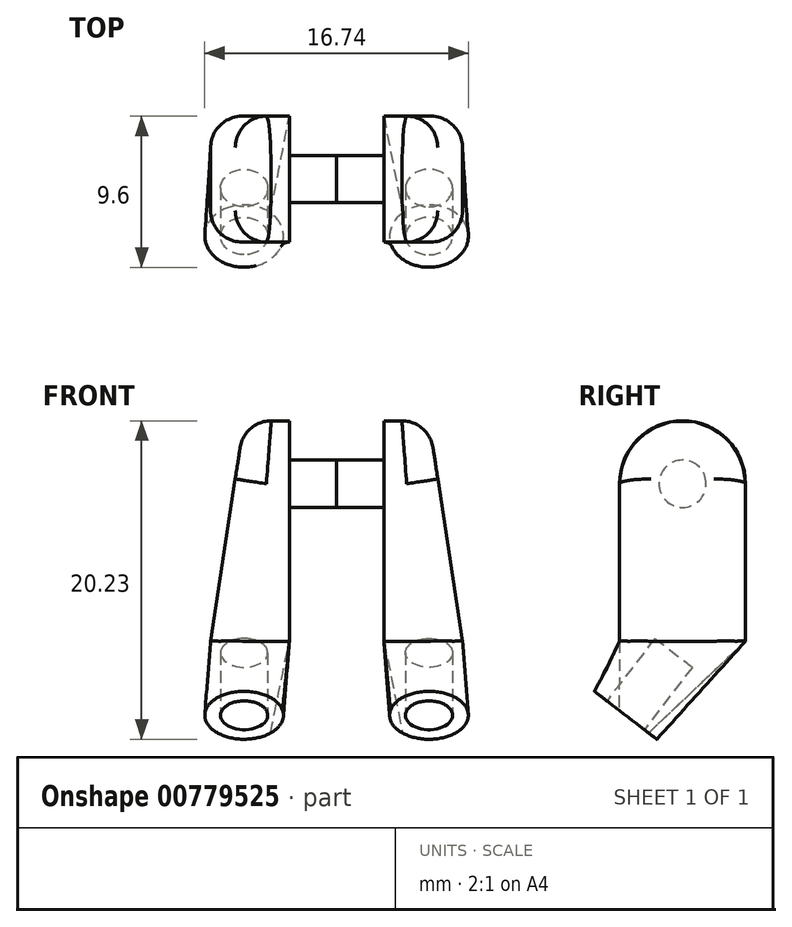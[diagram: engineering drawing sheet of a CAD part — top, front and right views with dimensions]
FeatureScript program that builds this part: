
annotation { "Feature Type Name" : "Feature", "Feature Type Description" : "" }
export const myFeature = defineFeature(function(context is Context, id is Id, definition is map)
    precondition{}
    {
        {
            var Q0;
            Q0=qCreatedBy(makeId("Right.planeOp"),FACE);
            var sketch = newSketch(context, id + "F0", { "sketchPlane" : qUnion([Q0])});
            skCircle(sketch, "E0", {"center": v(-23.98, 9.36) * mm, "radius": 1.5 * mm});
            skSolve(sketch);
        }
        {
            var Q0;
            Q0 = qSketchRegion(id + "F0", true);
            extrude(context, id + "F1", {"entities" : qUnion([Q0]), "depth" : 3 * mm, "offsetDistance" : 25 * mm});
        }
        {
            var Q0;
            Q0=makeQuery(id+"F1.opExtrude","CAP_FACE",FACE,{"disambiguationData":[OSD([sQuery(id+"F0.wireOp",EDGE,"E0")])],"isStart":false});
            var sketch = newSketch(context, id + "F2", { "sketchPlane" : qUnion([Q0])});
            skArc(sketch, "E1", {"start": v(-19.98, 9.36) * mm, "mid": v(-23.98, 13.36) * mm, "end": v(-27.98, 9.36) * mm});
            skLineSegment(sketch, "E2.top", {"start": v(-19.98, -0.64) * mm, "end": v(-27.98, -0.64) * mm});
            skLineSegment(sketch, "E2.left", {"start": v(-19.98, 9.36) * mm, "end": v(-19.98, -0.64) * mm});
            skLineSegment(sketch, "E2.right", {"start": v(-27.98, 9.36) * mm, "end": v(-27.98, -0.64) * mm});
            skPoint(sketch, "E2.middle", {"position": v(-23.98, 4.36) * mm});
            skLineSegment(sketch, "E3", {"start": v(-19.98, -0.64) * mm, "end": v(-25.08, -7.28) * mm, "construction": true});
            skLineSegment(sketch, "E4", {"start": v(-25.08, -7.28) * mm, "end": v(-30.1, -3.41) * mm, "construction": true});
            skLineSegment(sketch, "E5", {"start": v(-30.1, -3.41) * mm, "end": v(-27.98, -0.64) * mm, "construction": true});
            skLineSegment(sketch, "E6", {"start": v(-27.6, -5.34) * mm, "end": v(-26.14, -3.45) * mm, "construction": true});
            skSolve(sketch);
        }
        {
            var Q0;
            Q0 = qSketchRegion(id + "F2", true);
            extrude(context, id + "F3", {"entities" : qUnion([Q0]), "operationType" : NewBodyOperationType.ADD, "depth" : 5 * mm, "offsetDistance" : 25 * mm});
        }
        {
            var Q0;
            Q0=makeQuery(id+"F3.opExtrude","SWEPT_FACE",FACE,{"disambiguationData":[OSD([sQuery(id+"F2.wireOp",EDGE,"E2.right")])]});
            var sketch = newSketch(context, id + "F4", { "sketchPlane" : qUnion([Q0])});
            skLineSegment(sketch, "E7", {"start": v(8, -0.64) * mm, "end": v(5.63, 14.92) * mm});
            skLineSegment(sketch, "E8", {"start": v(5.63, 14.92) * mm, "end": v(9.74, 14.92) * mm});
            skLineSegment(sketch, "E9", {"start": v(9.74, 14.92) * mm, "end": v(8, -0.64) * mm});
            skSolve(sketch);
        }
        {
            var Q0;
            Q0 = qSketchRegion(id + "F4", true);
            extrude(context, id + "F5", {"entities" : qUnion([Q0]), "operationType" : NewBodyOperationType.REMOVE, "oppositeDirection" : true, "depth" : 25 * mm, "offsetDistance" : 25 * mm});
        }
        {
            var Q0;
            Q0=makeQuery(id+"F5.boolean.opBoolean","INTERSECT",EDGE,{"derivedFrom":[makeQuery(id+"F3.opExtrude","SWEPT_FACE",FACE,{"disambiguationData":[OSD([sQuery(id+"F2.wireOp",EDGE,"E1")])]}),makeQuery(id+"F5.opExtrude","SWEPT_FACE",FACE,{"disambiguationData":[OSD([sQuery(id+"F4.wireOp",EDGE,"E7")])]})]});
            var Q1;
            Q1=makeQuery(id+"F5.boolean.opBoolean","COPY",EDGE,{"derivedFrom":makeQuery(id+"F5.opExtrude","CAP_EDGE",EDGE,{"disambiguationData":[OSD([sQuery(id+"F4.wireOp",EDGE,"E7")])],"isStart":true})});
            fillet(context, id + "F6", {"entities" : qUnion([Q0, Q1]), "radius" : 2 * mm, "tangentPropagation" : true, "allowEdgeOverflow" : false});
        }
        {
            var Q0;
            Q0=sQuery(id+"F2.wireOp",VERTEX,"E4.end");
            var Q1;
            Q1=sQuery(id+"F2.wireOp",EDGE,"E5");
            cPlane(context, id + "F7", {"entities" : qUnion([Q0, Q1]), "cplaneType" : CPlaneType.LINE_POINT, "offset" : 25 * mm, "width" : 150 * mm, "height" : 150 * mm});
        }
        {
            var Q0;
            Q0=qCreatedBy(id+"F7.planeOp",FACE);
            var sketch = newSketch(context, id + "F8", { "sketchPlane" : qUnion([Q0])});
            skLineSegment(sketch, "E10", {"start": v(3, -18.63) * mm, "end": v(12.44, -18.63) * mm, "construction": true});
            skCircle(sketch, "E11", {"center": v(5.87, -18.63) * mm, "radius": 2.5 * mm});
            skSolve(sketch);
        }
        {
            var Q1;
            Q1=makeQuery(id+"F3.opExtrude","SWEPT_FACE",FACE,{"disambiguationData":[OSD([sQuery(id+"F2.wireOp",EDGE,"E2.top")])]});
            var Q2;
            Q2=makeQuery(id+"F8.imprint","IMPRINT",FACE,{"disambiguationData":[TD([[makeQuery(id+"F8.imprint","IMPRINT",EDGE,{"derivedFrom":sQuery(id+"F8.wireOp",EDGE,"E11")}),1.0]])]});
            loft(context, id + "F9", {"operationType" : NewBodyOperationType.ADD, "sheetProfilesArray" : [{ "sheetProfileEntities" : qUnion([Q1]) }, { "sheetProfileEntities" : qUnion([Q2]) }]});
        }
        {
            var Q0;
            Q0=makeQuery(id+"F8.imprint","IMPRINT",FACE,{"disambiguationData":[TD([[makeQuery(id+"F8.imprint","IMPRINT",EDGE,{"derivedFrom":sQuery(id+"F8.wireOp",EDGE,"E11")}),1.0]])]});
            var sketch = newSketch(context, id + "F10", { "sketchPlane" : qUnion([Q0])});
            skCircle(sketch, "E12", {"center": v(5.87, -18.63) * mm, "radius": 1.5 * mm});
            skSolve(sketch);
        }
        {
            var Q0;
            Q0 = qSketchRegion(id + "F10", true);
            extrude(context, id + "F11", {"entities" : qUnion([Q0]), "operationType" : NewBodyOperationType.REMOVE, "depth" : 5 * mm, "offsetDistance" : 25 * mm});
        }
        {
            var Q0;
            Q0=makeQuery(id+"F1.opExtrude","SWEPT_BODY",BODY,{"disambiguationData":[OSD([sQuery(id+"F0.wireOp",EDGE,"E0")])]});
            var Q1;
            Q1=makeQuery(id+"F1.opExtrude","CAP_FACE",FACE,{"disambiguationData":[OSD([sQuery(id+"F0.wireOp",EDGE,"E0")])],"isStart":true});
            mirror(context, id + "F12", {"entities" : qUnion([Q0]), "mirrorPlane" : qUnion([Q1])});
        }
    });
